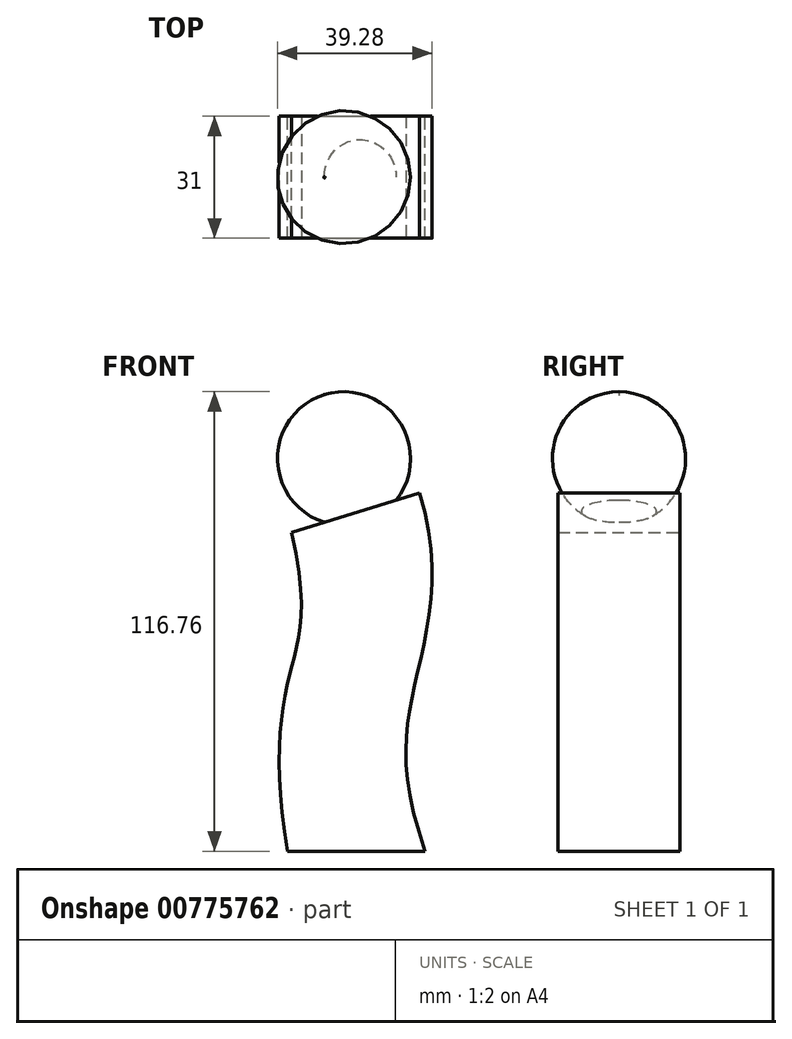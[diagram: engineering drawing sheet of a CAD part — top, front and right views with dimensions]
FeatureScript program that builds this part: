
annotation { "Feature Type Name" : "Feature", "Feature Type Description" : "" }
export const myFeature = defineFeature(function(context is Context, id is Id, definition is map)
    precondition{}
    {
        {
            var Q0;
            Q0=qCreatedBy(makeId("Front.planeOp"),FACE);
            var sketch = newSketch(context, id + "F0", { "sketchPlane" : qUnion([Q0])});
            skLineSegment(sketch, "E0", {"start": v(-5.69, -55.46) * mm, "end": v(29.31, -55.46) * mm});
            skFitSpline(sketch, "E1", {"points": [v(-5.69, -55.46) * mm, v(-5.11, -10.31) * mm, v(-4.69, 25.6) * mm], "startDerivative": vector(-21.07, 120.38) * mm, "endDerivative": vector(-29.83, 133.7) * mm});
            skLineSegment(sketch, "E2", {"start": v(-4.69, 25.6) * mm, "end": v(27.83, 35.54) * mm});
            skFitSpline(sketch, "E3", {"points": [v(27.83, 35.54) * mm, v(26.7, -12.86) * mm, v(29.31, -55.46) * mm], "startDerivative": vector(36.87, -114.83) * mm, "endDerivative": vector(42.37, -122.56) * mm});
            skArc(sketch, "E4", {"start": v(22.08, 33.78) * mm, "mid": v(3.8, 60.61) * mm, "end": v(3.64, 28.15) * mm});
            skLineSegment(sketch, "E5", {"start": v(12.77, 30.94) * mm, "end": v(3.7, 60.58) * mm});
            skSolve(sketch);
        }
        {
            var Q0;
            Q0=makeQuery(id+"F0.imprint","IMPRINT",FACE,{"disambiguationData":[TD([[makeQuery(id+"F0.imprint","IMPRINT",EDGE,{"derivedFrom":sQuery(id+"F0.wireOp",EDGE,"E0")}),1.0]])]});
            extrude(context, id + "F1", {"entities" : qUnion([Q0]), "endBound" : BoundingType.SYMMETRIC, "depth" : 31 * mm, "offsetDistance" : 25 * mm});
        }
        {
            var Q0;
            {var subQ3=sQuery(id+"F0.wireOp",EDGE,"E5");Q0=makeQuery(id+"F0.imprint","IMPRINT",FACE,{"disambiguationData":[TD([[makeQuery(id+"F0.imprint","IMPRINT",EDGE,{"derivedFrom":subQ3}),1.0]])]});}
            var Q1;
            Q1=sQuery(id+"F0.wireOp",EDGE,"E5");
            revolve(context, id + "F2", {"operationType" : NewBodyOperationType.ADD, "surfaceOperationType" : NewSurfaceOperationType.NEW, "entities" : qUnion([Q0]), "axis" : qUnion([Q1]), "revolveType" : RevolveType.FULL});
        }
    });
